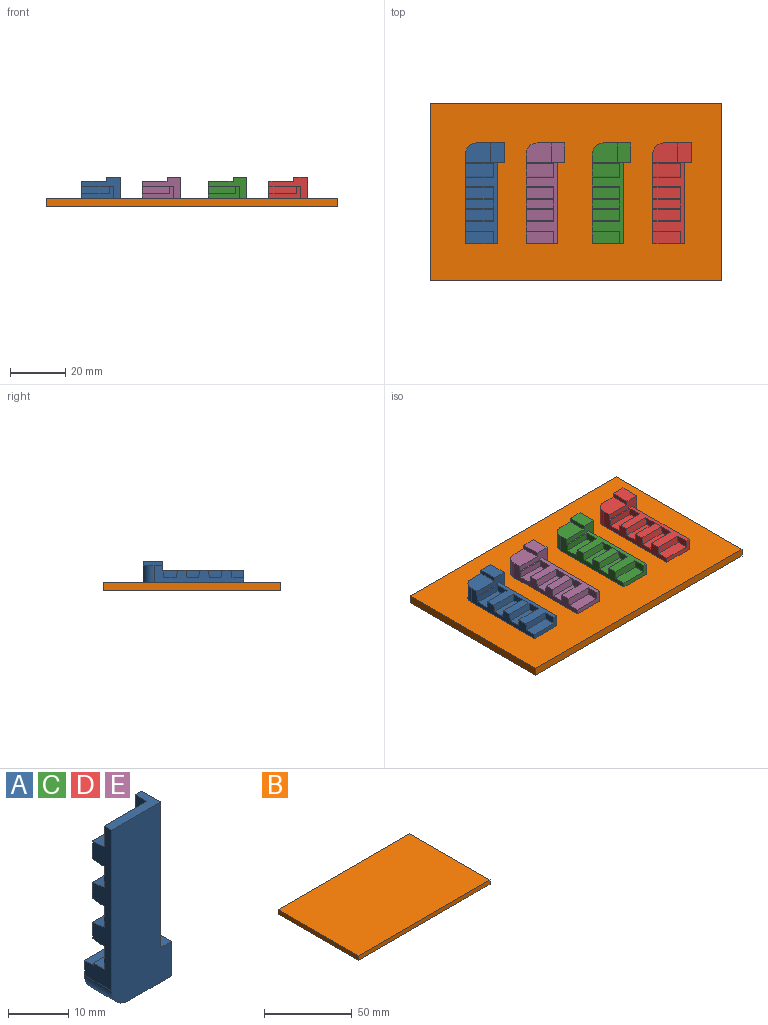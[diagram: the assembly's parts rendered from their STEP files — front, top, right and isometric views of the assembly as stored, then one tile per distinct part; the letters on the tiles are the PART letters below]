
ASSEMBLY  parts=5 mates=4
PART A: 29 faces, bbox 14x7.8x36.5 mm
  f0: plane 14x7.8mm, normal (0,0,1), area 46.5mm2, adj f1,f3,f4,f7,f18,f22,f23,f26
  f1: plane 32.5x6.3mm, normal (-1,0,0), area 101.2mm2, adj f0,f2,f5,f6,f7,f8,f9,f10
  f2: cylinder r=4mm len=6.3mm, axis (0,1,0), area 39.6mm2, adj f1,f19,f26,f28
  f3: plane 7x5mm, normal (0,1,0), area 35mm2, adj f0,f4,f19,f27
  f4: plane 7.8x7mm, normal (1,0,0), area 54.6mm2, adj f0,f3,f19,f26
  f5: plane 10x2.7mm, normal (0,0.06,1), area 27.1mm2, adj f1,f6,f18,f20
  f6: plane 10x4.2mm, normal (0,1,0), area 42mm2, adj f1,f5,f20,f25
  f7: plane 10x0.5mm, normal (0,1,0), area 5mm2, adj f0,f1,f8,f22
  f8: plane 10x2.5mm, normal (0,0,1), area 25mm2, adj f1,f7,f9,f22
  f9: plane 10x4.6mm, normal (0,1,0), area 46mm2, adj f1,f8,f10,f22
  f10: plane 10x2.7mm, normal (0,0.13,-0.99), area 27.2mm2, adj f1,f9,f18,f22
  f11: plane 10x2.7mm, normal (0,0.13,0.99), area 27.2mm2, adj f1,f12,f18,f21
  f12: plane 10x4.2mm, normal (0,1,0), area 42mm2, adj f1,f11,f13,f21
  f13: plane 10x2.7mm, normal (0,0.12,-0.99), area 27.2mm2, adj f1,f12,f14,f21
  f14: plane 10.01x3.21mm, normal (0,1,0), area 32mm2, adj f1,f13,f15,f18
  f15: plane 10x2.7mm, normal (0,0.14,0.99), area 27.2mm2, adj f1,f14,f16,f24
  f16: plane 10x4.2mm, normal (0,1,0), area 42mm2, adj f1,f15,f17,f24
  f17: plane 10x2.7mm, normal (0,0.09,-1), area 27.1mm2, adj f1,f16,f18,f24
  f18: plane 29.51x11.51mm, normal (0,1,0), area 112.2mm2, adj f0,f1,f5,f10,f11,f14,f17,f20
  f19: plane 10x7.8mm, normal (0,0,-1), area 70.5mm2, adj f2,f3,f4,f26,f27,f28
  f20: plane 4.37x2.7mm, normal (-1,0,0), area 11.6mm2, adj f5,f6,f18,f25
  f21: plane 4.88x2.7mm, normal (-1,0,0), area 12.3mm2, adj f11,f12,f13,f18
  f22: plane 5.45x2.7mm, normal (-1,0,0), area 13mm2, adj f0,f7,f8,f9,f10,f18
  f23: plane 29.5x4.45mm, normal (1,0,0), area 131.3mm2, adj f0,f18,f25,f26
  f24: plane 4.8x2.7mm, normal (-1,0,0), area 12.1mm2, adj f15,f16,f17,f18
  f25: plane 11.5x4.45mm, normal (0,0,1), area 24.2mm2, adj f1,f6,f18,f20,f23,f26
  f26: plane 36.5x14mm, normal (0,-1,0), area 433.8mm2, adj f0,f1,f2,f4,f19,f23,f25
  f27: plane 7x1.5mm, normal (-1,0,0), area 10.5mm2, adj f0,f3,f19,f28
  f28: plane 9x7mm, normal (0,1,0), area 59.6mm2, adj f0,f1,f2,f19,f27
PART B: 6 faces, bbox 106x64.5x3 mm
  f0: plane 106x3mm, normal (0,1,0), area 318mm2, adj f1,f3,f4,f5
  f1: plane 64.5x3mm, normal (-1,0,0), area 193.5mm2, adj f0,f2,f4,f5
  f2: plane 106x3mm, normal (0,-1,0), area 318mm2, adj f1,f3,f4,f5
  f3: plane 64.5x3mm, normal (1,0,0), area 193.5mm2, adj f0,f2,f4,f5
  f4: plane 106x64.5mm, normal (0,0,1), area 6837mm2, adj f0,f1,f2,f3
  f5: plane 106x64.5mm, normal (0,0,-1), area 6837mm2, adj f0,f1,f2,f3
PART C: same geometry as A
PART D: same geometry as A
PART E: same geometry as A
PLACE A rot(axis=(1,0,0),90deg) t=(-93.07,-14.46,11.8)mm
PLACE B t=(0,-64.5,0)mm
PLACE C rot(axis=(1,0,0),90deg) t=(-47.07,-14.46,11.8)mm
PLACE D rot(axis=(1,0,0),90deg) t=(-25.07,-14.46,11.8)mm
PLACE E rot(axis=(1,0,0),90deg) t=(-71.07,-14.46,11.8)mm
MATE fastened D.f26 <-> B.f4  axis (0,0,-1) through (-19,-32.25,3)mm
MATE fastened A.f26 <-> B.f4  axis (0,0,-1) through (-87,-32.25,3)mm
MATE fastened E.f26 <-> B.f4  axis (0,0,-1) through (-65,-32.25,3)mm
MATE fastened C.f26 <-> B.f4  axis (0,0,-1) through (-41,-32.25,3)mm
